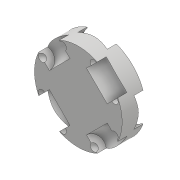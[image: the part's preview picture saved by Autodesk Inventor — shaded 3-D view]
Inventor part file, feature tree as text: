
AUTODESK INVENTOR PART (.ipt)
format: ipt  version: 2017 (Build 210142000, 142)  size: 193,024 bytes
history: native  units: mm
features: sketch x3, revolve x2, pattern_circular x2, extrude x1
ambient origin geometry x8: Origin, YZ Plane, XZ Plane, XY Plane, X Axis, Y Axis, Z Axis, Center Point
bodies: Solid1 (feature_tree)
feature tree (8):
  extrude  "Extrusion1"  Depth=16.0mm TaperAngle=0.0deg
  revolve  "Revolution1"  [1 undecoded]
  pattern_circular  "Circular Pattern2"  [2 undecoded]
  revolve  "Revolution2"  [1 undecoded]
  pattern_circular  "Circular Pattern3"  Count=2  [1 undecoded]
  sketch  "Sketch1"  dims[d0=60.0mm d1=16.0mm d2=0.0mm]
  sketch  "Sketch2"  dims[d3=14.0mm d4=25.0mm]
  sketch  "Sketch3"  dims[d5=6.0mm d6=5.0mm d7=5.0mm d8=20.0mm d9=90.0deg d13=40.0mm d14=360.0deg d16=45.0deg d17=25.0mm d18=14.0mm d19=20.0mm d20=5.0mm d21=5.0mm d22=90.0deg d23=40.0mm d24=360.0deg]
note: 5 required parameter values undecoded (feature->parameter linkage not recoverable at this tier; creation-order binding heuristic only, values carry confidence <= 0.55)